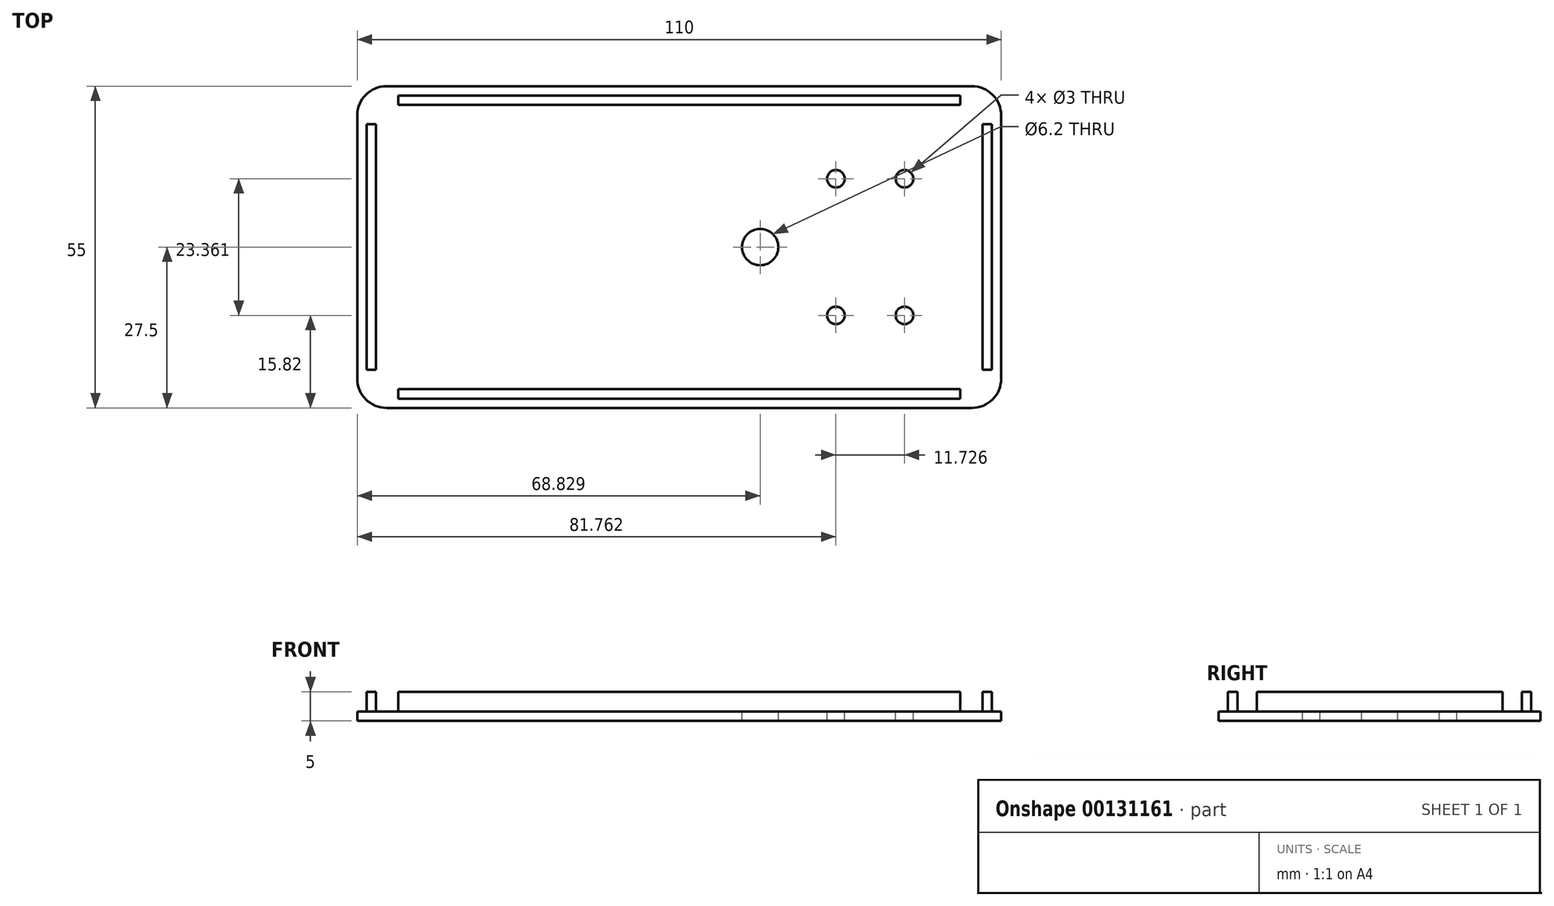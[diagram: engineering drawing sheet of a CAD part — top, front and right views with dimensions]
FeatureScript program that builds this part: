
annotation { "Feature Type Name" : "Feature", "Feature Type Description" : "" }
export const myFeature = defineFeature(function(context is Context, id is Id, definition is map)
    precondition{}
    {
        {
            var Q0;
            Q0=qCreatedBy(makeId("Top.planeOp"),FACE);
            var sketch = newSketch(context, id + "F0", { "sketchPlane" : qUnion([Q0])});
            skLineSegment(sketch, "E0.bottom", {"start": v(55, -27.5) * mm, "end": v(-55, -27.5) * mm});
            skLineSegment(sketch, "E0.top", {"start": v(55, 27.5) * mm, "end": v(-55, 27.5) * mm});
            skLineSegment(sketch, "E0.left", {"start": v(55, -27.5) * mm, "end": v(55, 27.5) * mm});
            skLineSegment(sketch, "E0.right", {"start": v(-55, -27.5) * mm, "end": v(-55, 27.5) * mm});
            skPoint(sketch, "E0.middle", {"position": v(0, 0) * mm});
            skSolve(sketch);
        }
        {
            var Q0;
            Q0=qSketchRegion(id+"F0",true);
            extrude(context, id + "F1", {"entities" : qUnion([Q0]), "depth" : 1.6 * mm});
        }
        {
            var Q0;
            Q0=makeQuery(id+"F1.opExtrude","CAP_FACE",FACE,{"disambiguationData":[OSD([sQuery(id+"F0.wireOp",EDGE,"E0.bottom"),sQuery(id+"F0.wireOp",EDGE,"E0.top"),sQuery(id+"F0.wireOp",EDGE,"E0.left"),sQuery(id+"F0.wireOp",EDGE,"E0.right")])],"isStart":false});
            var sketch = newSketch(context, id + "F2", { "sketchPlane" : qUnion([Q0])});
            skLineSegment(sketch, "E1", {"start": v(55, 0) * mm, "end": v(-55, 0) * mm, "construction": true});
            skLineSegment(sketch, "E2", {"start": v(0, -27.5) * mm, "end": v(0, 27.5) * mm, "construction": true});
            skLineSegment(sketch, "E3.bottom", {"start": v(-48, 25.9) * mm, "end": v(48, 25.9) * mm});
            skLineSegment(sketch, "E3.top", {"start": v(-48, 24.3) * mm, "end": v(48, 24.3) * mm});
            skLineSegment(sketch, "E3.left", {"start": v(-48, 25.9) * mm, "end": v(-48, 24.3) * mm});
            skLineSegment(sketch, "E3.right", {"start": v(48, 25.9) * mm, "end": v(48, 24.3) * mm});
            skLineSegment(sketch, "E4.bottom", {"start": v(51.8, 21) * mm, "end": v(53.4, 21) * mm});
            skLineSegment(sketch, "E4.top", {"start": v(51.8, -21) * mm, "end": v(53.4, -21) * mm});
            skLineSegment(sketch, "E4.left", {"start": v(51.8, 21) * mm, "end": v(51.8, -21) * mm});
            skLineSegment(sketch, "E4.right", {"start": v(53.4, 21) * mm, "end": v(53.4, -21) * mm});
            skLineSegment(sketch, "E5.MirrorCS", {"start": v(-48, -24.3) * mm, "end": v(48, -24.3) * mm});
            skLineSegment(sketch, "E6.MirrorCS", {"start": v(-48, -25.9) * mm, "end": v(48, -25.9) * mm});
            skLineSegment(sketch, "E7.MirrorCS", {"start": v(-48, -25.9) * mm, "end": v(-48, -24.3) * mm});
            skLineSegment(sketch, "E8.MirrorCS", {"start": v(48, -25.9) * mm, "end": v(48, -24.3) * mm});
            skLineSegment(sketch, "E9.MirrorCS", {"start": v(-51.8, 21) * mm, "end": v(-51.8, -21) * mm});
            skLineSegment(sketch, "E10.MirrorCS", {"start": v(-53.4, 21) * mm, "end": v(-53.4, -21) * mm});
            skLineSegment(sketch, "E11.MirrorCS", {"start": v(-51.8, 21) * mm, "end": v(-53.4, 21) * mm});
            skLineSegment(sketch, "E12.MirrorCS", {"start": v(-51.8, -21) * mm, "end": v(-53.4, -21) * mm});
            skLineSegment(sketch, "E13.bottom", {"start": v(38.49, -11.68) * mm, "end": v(26.76, -11.68) * mm, "construction": true});
            skLineSegment(sketch, "E13.top", {"start": v(38.49, 11.68) * mm, "end": v(26.76, 11.68) * mm, "construction": true});
            skLineSegment(sketch, "E13.left", {"start": v(38.49, -11.68) * mm, "end": v(38.49, 11.68) * mm, "construction": true});
            skLineSegment(sketch, "E13.right", {"start": v(26.76, -11.68) * mm, "end": v(26.76, 11.68) * mm, "construction": true});
            skPoint(sketch, "E13.middle", {"position": v(32.63, 0) * mm});
            skCircle(sketch, "E14", {"center": v(26.76, 11.68) * mm, "radius": 1.5 * mm});
            skCircle(sketch, "E15", {"center": v(38.49, 11.68) * mm, "radius": 1.5 * mm});
            skCircle(sketch, "E16", {"center": v(26.76, -11.68) * mm, "radius": 1.5 * mm});
            skCircle(sketch, "E17", {"center": v(38.49, -11.68) * mm, "radius": 1.5 * mm});
            skCircle(sketch, "E18", {"center": v(13.83, 0) * mm, "radius": 3.1 * mm});
            skSolve(sketch);
        }
        {
            var Q0;
            Q0=makeQuery(id+"F2.imprint","IMPRINT",FACE,{"disambiguationData":[TD([[makeQuery(id+"F2.imprint","IMPRINT",EDGE,{"derivedFrom":sQuery(id+"F2.wireOp",EDGE,"E14")}),1.0]])]});
            var Q1;
            Q1=makeQuery(id+"F2.imprint","IMPRINT",FACE,{"disambiguationData":[TD([[makeQuery(id+"F2.imprint","IMPRINT",EDGE,{"derivedFrom":sQuery(id+"F2.wireOp",EDGE,"E15")}),1.0]])]});
            var Q2;
            Q2=makeQuery(id+"F2.imprint","IMPRINT",FACE,{"disambiguationData":[TD([[makeQuery(id+"F2.imprint","IMPRINT",EDGE,{"derivedFrom":sQuery(id+"F2.wireOp",EDGE,"E16")}),1.0]])]});
            var Q3;
            Q3=makeQuery(id+"F2.imprint","IMPRINT",FACE,{"disambiguationData":[TD([[makeQuery(id+"F2.imprint","IMPRINT",EDGE,{"derivedFrom":sQuery(id+"F2.wireOp",EDGE,"E17")}),1.0]])]});
            var Q4;
            Q4=makeQuery(id+"F2.imprint","IMPRINT",FACE,{"disambiguationData":[TD([[makeQuery(id+"F2.imprint","IMPRINT",EDGE,{"derivedFrom":sQuery(id+"F2.wireOp",EDGE,"E18")}),1.0]])]});
            extrude(context, id + "F3", {"entities" : qUnion([Q0, Q1, Q2, Q3, Q4]), "operationType" : NewBodyOperationType.REMOVE, "endBound" : BoundingType.UP_TO_NEXT, "oppositeDirection" : true, "depth" : 25 * mm, "offsetDistance" : 25 * mm});
        }
        {
            var Q0;
            Q0=makeQuery(id+"F2.imprint","IMPRINT",FACE,{"disambiguationData":[TD([[makeQuery(id+"F2.imprint","IMPRINT",EDGE,{"derivedFrom":sQuery(id+"F2.wireOp",EDGE,"E3.bottom")}),-1.0]])]});
            var Q1;
            Q1=makeQuery(id+"F2.imprint","IMPRINT",FACE,{"disambiguationData":[TD([[makeQuery(id+"F2.imprint","IMPRINT",EDGE,{"derivedFrom":sQuery(id+"F2.wireOp",EDGE,"E9.MirrorCS")}),-1.0]])]});
            var Q2;
            Q2=makeQuery(id+"F2.imprint","IMPRINT",FACE,{"disambiguationData":[TD([[makeQuery(id+"F2.imprint","IMPRINT",EDGE,{"derivedFrom":sQuery(id+"F2.wireOp",EDGE,"E5.MirrorCS")}),-1.0]])]});
            var Q3;
            Q3=makeQuery(id+"F2.imprint","IMPRINT",FACE,{"disambiguationData":[TD([[makeQuery(id+"F2.imprint","IMPRINT",EDGE,{"derivedFrom":sQuery(id+"F2.wireOp",EDGE,"E4.bottom")}),-1.0]])]});
            extrude(context, id + "F4", {"entities" : qUnion([Q0, Q1, Q2, Q3]), "operationType" : NewBodyOperationType.ADD, "depth" : 3.4 * mm});
        }
        {
            var Q0;
            Q0=makeQuery(id+"F1.opExtrude","SWEPT_EDGE",EDGE,{"disambiguationData":[OSD([sQuery(id+"F0.wireOp",EDGE,"E0.bottom"),sQuery(id+"F0.wireOp",EDGE,"E0.left")])]});
            var Q1;
            Q1=makeQuery(id+"F1.opExtrude","SWEPT_EDGE",EDGE,{"disambiguationData":[OSD([sQuery(id+"F0.wireOp",EDGE,"E0.bottom"),sQuery(id+"F0.wireOp",EDGE,"E0.right")])]});
            var Q2;
            Q2=makeQuery(id+"F1.opExtrude","SWEPT_EDGE",EDGE,{"disambiguationData":[OSD([sQuery(id+"F0.wireOp",EDGE,"E0.top"),sQuery(id+"F0.wireOp",EDGE,"E0.left")])]});
            var Q3;
            Q3=makeQuery(id+"F1.opExtrude","SWEPT_EDGE",EDGE,{"disambiguationData":[OSD([sQuery(id+"F0.wireOp",EDGE,"E0.top"),sQuery(id+"F0.wireOp",EDGE,"E0.right")])]});
            fillet(context, id + "F5", {"entities" : qUnion([Q0, Q1, Q2, Q3]), "radius" : 5 * mm, "tangentPropagation" : true, "allowEdgeOverflow" : false});
        }
    });
